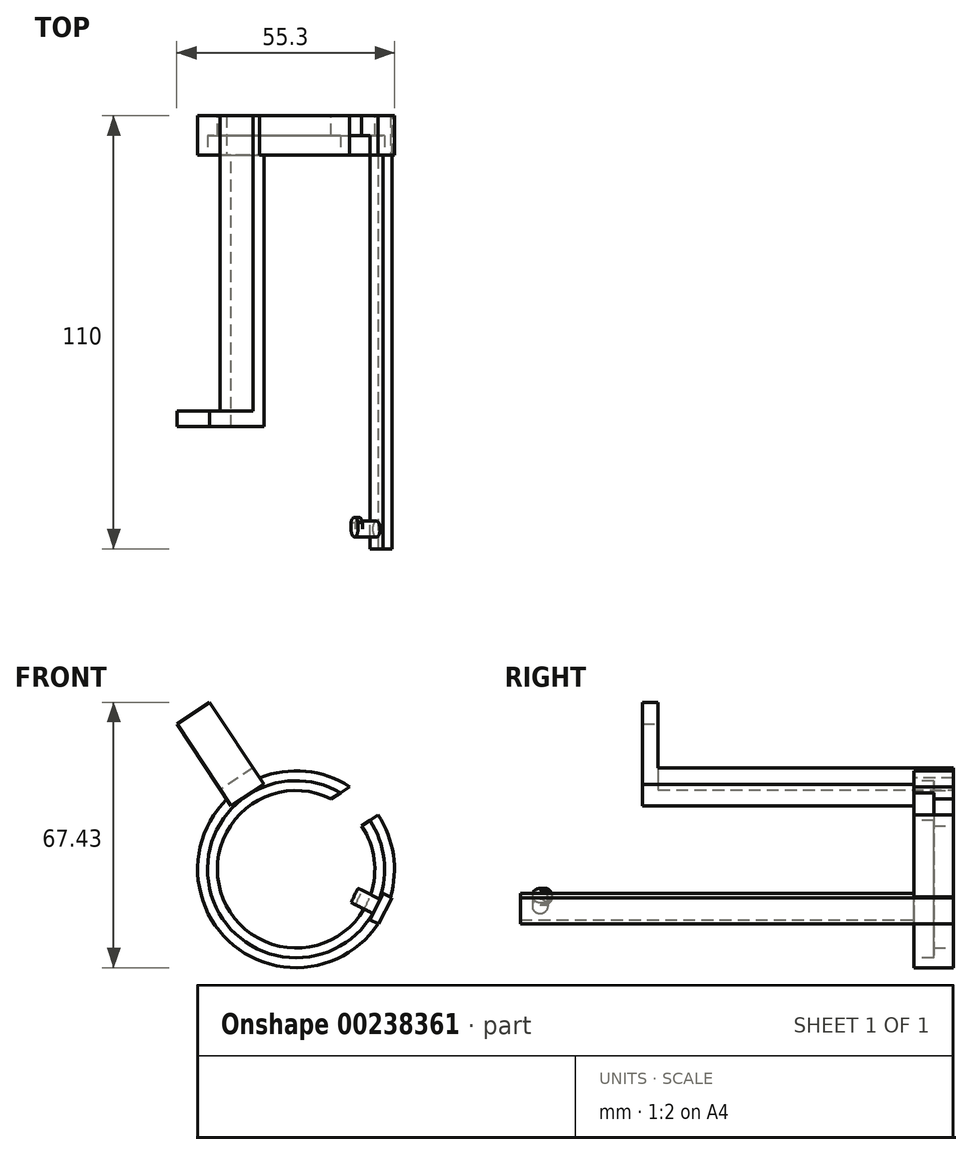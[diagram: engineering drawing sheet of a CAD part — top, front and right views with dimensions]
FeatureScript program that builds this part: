
annotation { "Feature Type Name" : "Feature", "Feature Type Description" : "" }
export const myFeature = defineFeature(function(context is Context, id is Id, definition is map)
    precondition{}
    {
        {
            var Q0;
            Q0=qCreatedBy(makeId("Front.planeOp"),FACE);
            var sketch = newSketch(context, id + "F0", { "sketchPlane" : qUnion([Q0])});
            skCircle(sketch, "E0", {"center": v(0, 0) * mm, "radius": 20 * mm});
            skCircle(sketch, "E1", {"center": v(0, 0) * mm, "radius": 23.5 * mm});
            skSolve(sketch);
        }
        {
            var Q0;
            Q0=makeQuery(id+"F0.imprint","IMPRINT",FACE,{"disambiguationData":[TD([[makeQuery(id+"F0.imprint","IMPRINT",EDGE,{"derivedFrom":sQuery(id+"F0.wireOp",EDGE,"E0")}),-1.0]])]});
            extrude(context, id + "F1", {"entities" : qUnion([Q0]), "depth" : 5 * mm});
        }
        {
            var Q0;
            Q0=qCreatedBy(makeId("Front.planeOp"),FACE);
            cPlane(context, id + "F2", {"entities" : qUnion([Q0]), "cplaneType" : CPlaneType.OFFSET, "offset" : 10 * mm, "width" : 150 * mm, "height" : 150 * mm});
        }
        {
            var Q0;
            Q0=qCreatedBy(id+"F2.planeOp",FACE);
            var sketch = newSketch(context, id + "F3", { "sketchPlane" : qUnion([Q0])});
            skCircle(sketch, "E2", {"center": v(0, 0) * mm, "radius": 22.5 * mm});
            skCircle(sketch, "E3", {"center": v(0, 0) * mm, "radius": 25 * mm});
            skSolve(sketch);
        }
        {
            var Q0;
            Q0=makeQuery(id+"F3.imprint","IMPRINT",FACE,{"disambiguationData":[TD([[makeQuery(id+"F3.imprint","IMPRINT",EDGE,{"derivedFrom":sQuery(id+"F3.wireOp",EDGE,"E2")}),-1.0]])]});
            extrude(context, id + "F4", {"entities" : qUnion([Q0]), "oppositeDirection" : true, "depth" : 10 * mm});
        }
        {
            var Q0;
            Q0=qCreatedBy(makeId("Front.planeOp"),FACE);
            var sketch = newSketch(context, id + "F5", { "sketchPlane" : qUnion([Q0])});
            skLineSegment(sketch, "E4", {"start": v(27.66, -0.58) * mm, "end": v(17.66, -0.58) * mm});
            skLineSegment(sketch, "E5.bottom", {"start": v(24.33, -7.24) * mm, "end": v(22.1, -6.12) * mm});
            skLineSegment(sketch, "E5.top", {"start": v(21, -13.9) * mm, "end": v(18.76, -12.8) * mm});
            skLineSegment(sketch, "E5.left", {"start": v(24.33, -7.24) * mm, "end": v(21, -13.9) * mm});
            skLineSegment(sketch, "E5.right", {"start": v(22.1, -6.12) * mm, "end": v(18.76, -12.8) * mm});
            skLineSegment(sketch, "E6", {"start": v(17.66, -0.58) * mm, "end": v(17.66, -20.58) * mm});
            skLineSegment(sketch, "E7", {"start": v(17.66, -20.58) * mm, "end": v(27.66, -20.58) * mm});
            skLineSegment(sketch, "E8", {"start": v(27.66, -20.58) * mm, "end": v(27.66, -0.58) * mm});
            skSolve(sketch);
        }
        {
            var Q0;
            Q0=makeQuery(id+"F5.imprint","IMPRINT",FACE,{"disambiguationData":[TD([[makeQuery(id+"F5.imprint","IMPRINT",EDGE,{"derivedFrom":sQuery(id+"F5.wireOp",EDGE,"E5.bottom")}),1.0]])]});
            extrude(context, id + "F6", {"entities" : qUnion([Q0]), "operationType" : NewBodyOperationType.ADD, "offsetDistance" : 25 * mm, "depth" : 110 * mm});
        }
        {
            var Q0;
            Q0=makeQuery(id+"F6.opExtrude","SWEPT_FACE",FACE,{"disambiguationData":[OSD([sQuery(id+"F5.wireOp",EDGE,"E5.left")])]});
            cPlane(context, id + "F7", {"entities" : qUnion([Q0]), "cplaneType" : CPlaneType.OFFSET, "offset" : 2.5 * mm, "oppositeDirection" : true, "width" : 150 * mm, "height" : 150 * mm});
        }
        {
            var Q0;
            Q0=qCreatedBy(id+"F7.planeOp",FACE);
            var sketch = newSketch(context, id + "F8", { "sketchPlane" : qUnion([Q0])});
            skLineSegment(sketch, "E9.bottom", {"start": v(-10, 4.41) * mm, "end": v(0, 4.41) * mm});
            skLineSegment(sketch, "E9.top", {"start": v(-10, -3.04) * mm, "end": v(0, -3.04) * mm});
            skLineSegment(sketch, "E9.left", {"start": v(-10, 4.41) * mm, "end": v(-10, -3.04) * mm});
            skLineSegment(sketch, "E9.right", {"start": v(0, 4.41) * mm, "end": v(0, -3.04) * mm});
            skSolve(sketch);
        }
        {
            var Q0;
            Q0=makeQuery(id+"F8.imprint","IMPRINT",FACE,{"disambiguationData":[TD([[makeQuery(id+"F8.imprint","IMPRINT",EDGE,{"derivedFrom":sQuery(id+"F8.wireOp",EDGE,"E9.bottom")}),-1.0]])]});
            extrude(context, id + "F9", {"entities" : qUnion([Q0]), "oppositeDirection" : true, "depth" : 2.5 * mm});
        }
        {
            var Q0;
            Q0=qCreatedBy(id+"F7.planeOp",FACE);
            var sketch = newSketch(context, id + "F10", { "sketchPlane" : qUnion([Q0])});
            skCircle(sketch, "E10", {"center": v(-105, 0.7) * mm, "radius": 2 * mm});
            skSolve(sketch);
        }
        {
            var Q0;
            Q0=qCreatedBy(makeId("Front.planeOp"),FACE);
            var sketch = newSketch(context, id + "F11", { "sketchPlane" : qUnion([Q0])});
            skLineSegment(sketch, "E11.bottom", {"start": v(-10.93, 25.74) * mm, "end": v(-19.28, 20.23) * mm});
            skLineSegment(sketch, "E11.top", {"start": v(-8.18, 21.56) * mm, "end": v(-16.52, 16.05) * mm});
            skLineSegment(sketch, "E11.left", {"start": v(-10.93, 25.74) * mm, "end": v(-8.18, 21.56) * mm});
            skLineSegment(sketch, "E11.right", {"start": v(-19.28, 20.23) * mm, "end": v(-16.52, 16.05) * mm});
            skSolve(sketch);
        }
        {
            var Q0;
            Q0=makeQuery(id+"F11.imprint","IMPRINT",FACE,{"disambiguationData":[TD([[makeQuery(id+"F11.imprint","IMPRINT",EDGE,{"derivedFrom":sQuery(id+"F11.wireOp",EDGE,"E11.bottom")}),1.0]])]});
            extrude(context, id + "F12", {"entities" : qUnion([Q0]), "operationType" : NewBodyOperationType.ADD, "offsetDistance" : 25 * mm, "depth" : 75 * mm});
        }
        {
            var Q0;
            Q0=makeQuery(id+"F12.opExtrude","SWEPT_FACE",FACE,{"disambiguationData":[OSD([sQuery(id+"F11.wireOp",EDGE,"E11.bottom")])]});
            var sketch = newSketch(context, id + "F13", { "sketchPlane" : qUnion([Q0])});
            skLineSegment(sketch, "E12.bottom", {"start": v(5.06, -79) * mm, "end": v(-4.94, -79) * mm});
            skLineSegment(sketch, "E12.top", {"start": v(5.06, -75) * mm, "end": v(-4.94, -75) * mm});
            skLineSegment(sketch, "E12.left", {"start": v(5.06, -79) * mm, "end": v(5.06, -75) * mm});
            skLineSegment(sketch, "E12.right", {"start": v(-4.94, -79) * mm, "end": v(-4.94, -75) * mm});
            skSolve(sketch);
        }
        {
            var Q0;
            Q0=makeQuery(id+"F9.opExtrude","SWEPT_BODY",BODY,{"disambiguationData":[OSD([sQuery(id+"F8.wireOp",EDGE,"E9.bottom"),sQuery(id+"F8.wireOp",EDGE,"E9.top"),sQuery(id+"F8.wireOp",EDGE,"E9.left"),sQuery(id+"F8.wireOp",EDGE,"E9.right")])]});
            deleteBodies(context, id + "F14", {"entities" : qUnion([Q0])});
        }
        {
            var Q0;
            Q0=makeQuery(id+"F10.imprint","IMPRINT",FACE,{"disambiguationData":[TD([[makeQuery(id+"F10.imprint","IMPRINT",EDGE,{"derivedFrom":sQuery(id+"F10.wireOp",EDGE,"E10")}),1.0]])]});
            extrude(context, id + "F15", {"entities" : qUnion([Q0]), "operationType" : NewBodyOperationType.ADD, "oppositeDirection" : true, "depth" : 5 * mm});
        }
        {
            var Q0;
            Q0=makeQuery(id+"F12.opExtrude","CAP_FACE",FACE,{"disambiguationData":[OSD([sQuery(id+"F11.wireOp",EDGE,"E11.bottom"),sQuery(id+"F11.wireOp",EDGE,"E11.top"),sQuery(id+"F11.wireOp",EDGE,"E11.left"),sQuery(id+"F11.wireOp",EDGE,"E11.right")])],"isStart":false});
            var sketch = newSketch(context, id + "F16", { "sketchPlane" : qUnion([Q0])});
            skLineSegment(sketch, "E13", {"start": v(-19.28, 20.23) * mm, "end": v(-16.52, 16.05) * mm});
            skLineSegment(sketch, "E14", {"start": v(-16.52, 16.05) * mm, "end": v(-8.18, 21.56) * mm});
            skLineSegment(sketch, "E15", {"start": v(-8.18, 21.56) * mm, "end": v(-10.93, 25.74) * mm});
            skLineSegment(sketch, "E16", {"start": v(-10.93, 25.74) * mm, "end": v(-19.28, 20.23) * mm});
            skSolve(sketch);
        }
        {
            var Q0;
            Q0=makeQuery(id+"F16.imprint","IMPRINT",FACE,{"disambiguationData":[TD([[makeQuery(id+"F16.imprint","IMPRINT",EDGE,{"derivedFrom":sQuery(id+"F16.wireOp",EDGE,"E13")}),1.0]])]});
            extrude(context, id + "F17", {"entities" : qUnion([Q0]), "operationType" : NewBodyOperationType.ADD, "depth" : 4 * mm});
        }
        {
            var Q0;
            Q0=makeQuery(id+"F13.imprint","IMPRINT",FACE,{"disambiguationData":[TD([[makeQuery(id+"F13.imprint","IMPRINT",EDGE,{"derivedFrom":sQuery(id+"F13.wireOp",EDGE,"E12.bottom")}),-1.0]])]});
            extrude(context, id + "F18", {"entities" : qUnion([Q0]), "operationType" : NewBodyOperationType.ADD, "offsetDistance" : 25 * mm, "depth" : 20 * mm});
        }
        {
            var Q0;
            Q0=makeQuery(id+"F15.opExtrude","CAP_FACE",FACE,{"disambiguationData":[OSD([sQuery(id+"F10.wireOp",EDGE,"E10")])],"isStart":false});
            var sketch = newSketch(context, id + "F19", { "sketchPlane" : qUnion([Q0])});
            skCircle(sketch, "E17", {"center": v(105, 0.7) * mm, "radius": 2 * mm});
            skPoint(sketch, "E17.first.point", {"position": v(103, 0.6) * mm});
            skPoint(sketch, "E17.second.point", {"position": v(107, 0.54) * mm});
            skPoint(sketch, "E17.third.point", {"position": v(103, 0.6) * mm});
            skLineSegment(sketch, "E18.bottom", {"start": v(107, -1.3) * mm, "end": v(102, -1.3) * mm});
            skLineSegment(sketch, "E18.top", {"start": v(107, 2.7) * mm, "end": v(102, 2.7) * mm});
            skLineSegment(sketch, "E18.left", {"start": v(107, -1.3) * mm, "end": v(107, 2.7) * mm});
            skLineSegment(sketch, "E18.right", {"start": v(102, -1.3) * mm, "end": v(102, 2.7) * mm});
            skArc(sketch, "E19", {"start": v(105, 2.7) * mm, "mid": v(102, 0.7) * mm, "end": v(105, -1.3) * mm});
            skSolve(sketch);
        }
        {
            var Q0;
            Q0=makeQuery(id+"F18.boolean.opBoolean","MERGE",FACE,{"derivedFrom":[makeQuery(id+"F17.boolean.opBoolean","MERGE",FACE,{"derivedFrom":[makeQuery(id+"F12.opExtrude","SWEPT_FACE",FACE,{"disambiguationData":[OSD([sQuery(id+"F11.wireOp",EDGE,"E11.left")])]}),makeQuery(id+"F17.opExtrude","SWEPT_FACE",FACE,{"disambiguationData":[OSD([sQuery(id+"F16.wireOp",EDGE,"E15")])]})]}),makeQuery(id+"F18.opExtrude","SWEPT_FACE",FACE,{"disambiguationData":[OSD([sQuery(id+"F13.wireOp",EDGE,"E12.left")])]})]});
            var sketch = newSketch(context, id + "F20", { "sketchPlane" : qUnion([Q0])});
            skLineSegment(sketch, "E20.bottom", {"start": v(-12.88, 10) * mm, "end": v(17.12, 10) * mm});
            skLineSegment(sketch, "E20.top", {"start": v(-12.88, 0) * mm, "end": v(17.12, 0) * mm});
            skLineSegment(sketch, "E20.left", {"start": v(-12.88, 10) * mm, "end": v(-12.88, 0) * mm});
            skLineSegment(sketch, "E20.right", {"start": v(17.12, 10) * mm, "end": v(17.12, 0) * mm});
            skSolve(sketch);
        }
        {
            var Q0;
            Q0=makeQuery(id+"F20.imprint","IMPRINT",FACE,{"disambiguationData":[TD([[makeQuery(id+"F20.imprint","IMPRINT",EDGE,{"derivedFrom":sQuery(id+"F20.wireOp",EDGE,"E20.bottom")}),-1.0]])]});
            extrude(context, id + "F21", {"entities" : qUnion([Q0]), "operationType" : NewBodyOperationType.REMOVE, "depth" : 64.2 * mm, "offsetDistance" : 25 * mm});
        }
        {
            var Q0;
            {var subQ0=sQuery(id+"F19.wireOp",EDGE,"E19");var subQ1=sQuery(id+"F19.wireOp",EDGE,"E18.top");var subQ2=makeQuery(id+"F19.imprint","INTERSECT",VERTEX,{"derivedFrom":[subQ1,subQ0]});Q0=makeQuery(id+"F19.imprint","IMPRINT",FACE,{"disambiguationData":[TD([[makeQuery(id+"F19.imprint","IMPRINT",EDGE,{"disambiguationData":[TD([[subQ2,-1.0]])],"derivedFrom":subQ0}),1.0]])]});}
            var Q1;
            {var subQ1=sQuery(id+"F19.wireOp",EDGE,"E17");var subQ3=makeQuery(id+"F19.imprint","INTERSECT",VERTEX,{"derivedFrom":[subQ1,sQuery(id+"F19.wireOp",EDGE,"E18.left")]});Q1=makeQuery(id+"F19.imprint","IMPRINT",FACE,{"disambiguationData":[TD([[makeQuery(id+"F19.imprint","IMPRINT",EDGE,{"disambiguationData":[TD([[subQ3,1.0]])],"derivedFrom":subQ1}),-1.0]])]});}
            extrude(context, id + "F22", {"entities" : qUnion([Q0, Q1]), "operationType" : NewBodyOperationType.ADD, "depth" : 1.25 * mm, "offsetDistance" : 25 * mm});
        }
    });
